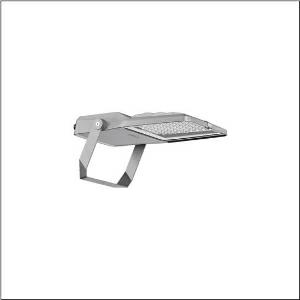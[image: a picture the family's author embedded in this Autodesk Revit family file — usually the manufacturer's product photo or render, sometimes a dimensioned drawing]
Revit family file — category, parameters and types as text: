
# Revit family: floodlight_fl_21_iq_mini___pl61_5xa7772d3c1a_e68f
name_source: partatom
category: Lighting Fixtures
units: mm (PartAtom-declared; Revit-internal decimal feet)

## family parameters
Cut with Voids When Loaded = No
Host = Face
Light Source = No
Part Type = Normal
Room Calculation Point = No
Round Connector Dimension = Use Diameter
Shared = No

## types (1)
- --- (1 x LED, 15060 lm, 143 W, 3000K)
    Apparent Load = 143 VA
    CIE Flux Codes = 33 65 98 100 100
    Color Rendering = 80
    Color Temperature = 3000K
    Default Elevation = 1800 mm
    Description = Floodlight FL 21 iQ mini, floodlight, primary light control with lens, of PMMA, primary optical cover: protective disc, of toughened safety glass, transparent, light distribution: PL61, light emission: direct distribution, installation type: surface-mounted, lamps: LED, High Power LED, rated values: 15.060lm | 143W | 105,3lm/W (begin service life); end service life: 15.060lm | 151,6W; at 50% lumin. flux: 7.530lm | 60,5W | 124,5lm/W, colour temperature: 3000K, colour rendering: CRI > 80, light colour: 830, light setting 1 begin service life: 100% | 15.060lm | 143W | 105,3lm/W | 3.000K, light setting 1 end service life: 151,6W, further light settings possible, control: Street-Remote, Auto-Match, Temp-Guard, Night-Set, Smart-Wire, Desk-Remote (wireless, voltage-free reading and setting of iQ features in the workshop via application-optimized NFC function/RFID function), optimised constant luminous flux control (CLO 2.0), pre-setting: linear dimming characteristic, with terminal, 6-pole, mains connection: 220..240V, AC, 50/60Hz, luminaire housing, of diecast aluminium, powder-coated, SITECO metallic grey (DB 702S), corrosivity category C5 mid according to DIN EN ISO 12944suitable for swimming poolschlorine-resistant, sealing non-destructively replaceable, mounting bracket, of steel, galvanised, powder-coated, SITECO metallic grey (DB 702S), protection rating (complete): IP66, insulation class (complete): insulation class II (safety insulation), certification: CE, ENEC, VDE, protection symbol: D, impact resistance: IK08, permissible operating ambient temperature: -40..+40°C, permissible operating ambient temperature for outdoor applications: -40..+50°C, standard: DIN EN 12944, LABS conformity tested according to VDMA 24364:2018-05, packaging unit: 1 piece

Light Distribution: PL61
    Height = 70 mm
    Lamp = 1 x LED
    Lamp Light Flux = 15060 lm
    Lamp Power = 143 W
    Lamp count = 1
    Length = 485 mm
    Luminous efficacy = 105 lm/W
    Manufacturer = Siteco
    ModVariant = No
    Model = 5XA7772D3C1A
    Number of Poles = 1
    OnlyDefault = Yes
    Power Factor = 1
    Product Name = Floodlight FL 21 iQ mini | PL61
    Product group = floodlight | pylon annexe
    ProductGroupID = 6201
    Protection Class = Protection class II
    Protection Degree = IP 66
    RLX_Detail_Level = 1
    RLX_Emergency_Light_Flux = 0 lm
    RLX_Emergency_Type = 0
    RLX_Emergency_Type_DB = No
    RlxData = <blob elided: 96865 chars, md5=409e01c1>
    Socket = socket
    Standby Power = 0 W
    System Light Flux = 15060 lm
    System Power = 143 W
    Type Comments = factory setting: luminous flux: 100 % | dim-lin: 254 | 730 mA
    Type Image = l_1006845.jpg
    URL = http://relux.com
    VarID = @adj_171899
    Voltage = 0 V
    Weight = 0.00 kg
    Width = 337 mm

## geometry (parser evidence)
native form markers: Blend x4, Sweep x13
no freeform markers — native parametric forms only
